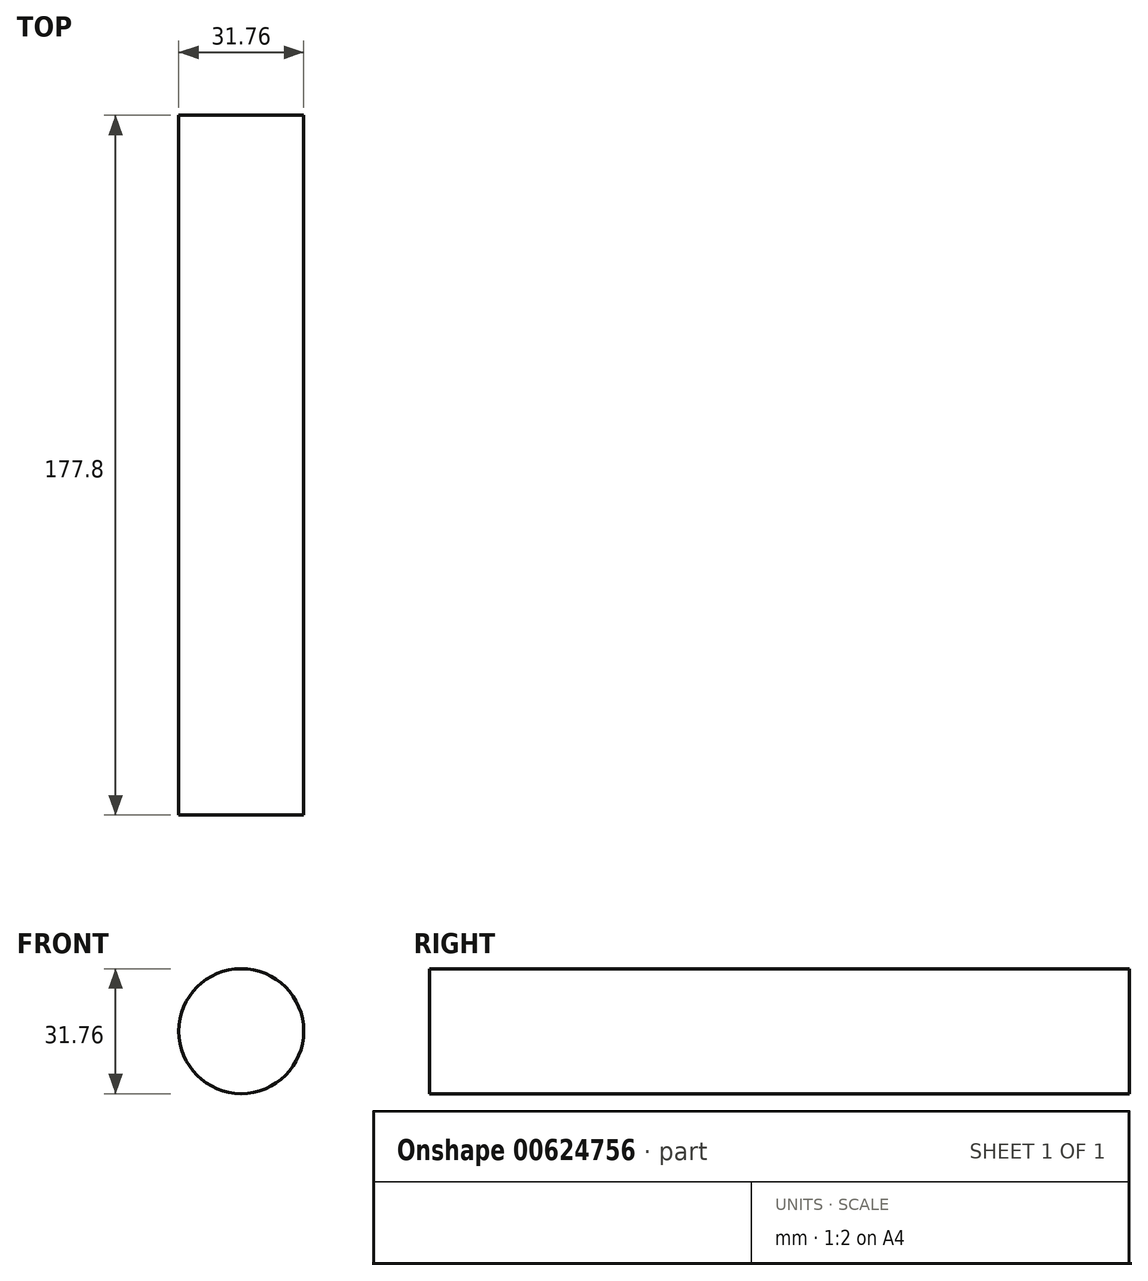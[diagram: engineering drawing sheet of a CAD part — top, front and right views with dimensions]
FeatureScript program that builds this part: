
annotation { "Feature Type Name" : "Feature", "Feature Type Description" : "" }
export const myFeature = defineFeature(function(context is Context, id is Id, definition is map)
    precondition{}
    {
        {
            var Q0;
            Q0=qCreatedBy(makeId("Front.planeOp"),FACE);
            var sketch = newSketch(context, id + "F0", { "sketchPlane" : qUnion([Q0])});
            skCircle(sketch, "E0", {"center": v(0, 0) * mm, "radius": 15.88 * mm});
            skSolve(sketch);
        }
        {
            var Q0;
            Q0 = qSketchRegion(id + "F0", true);
            extrude(context, id + "F1", {"entities" : qUnion([Q0]), "endBound" : BoundingType.SYMMETRIC, "depth" : 177.8 * mm, "offsetDistance" : 25.4 * mm});
        }
    });
